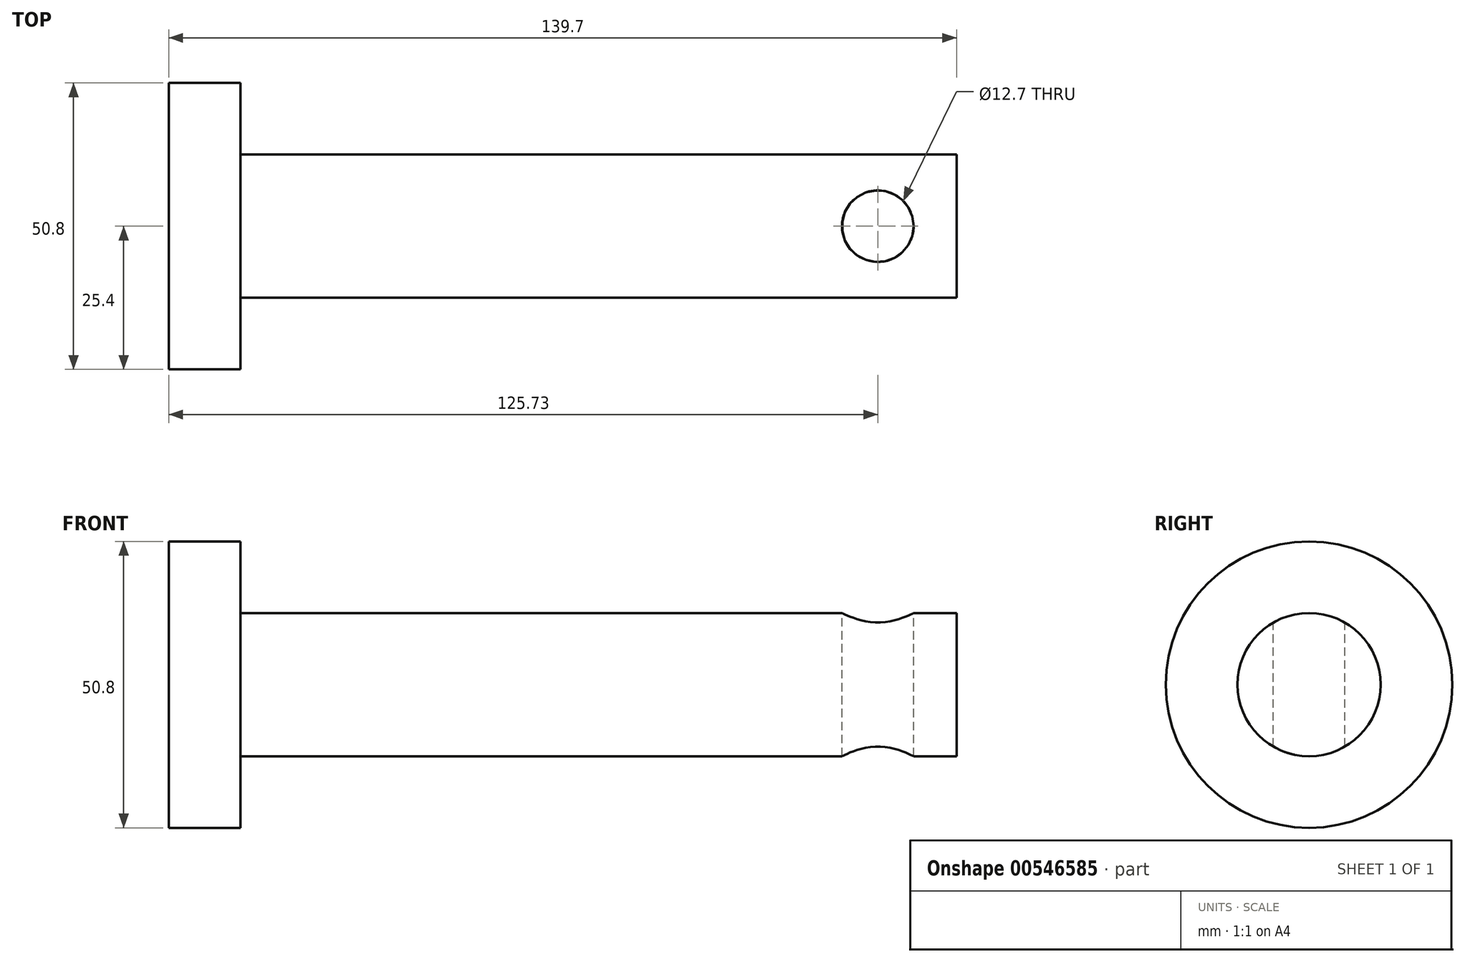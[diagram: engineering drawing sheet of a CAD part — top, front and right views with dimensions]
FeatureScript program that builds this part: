
annotation { "Feature Type Name" : "Feature", "Feature Type Description" : "" }
export const myFeature = defineFeature(function(context is Context, id is Id, definition is map)
    precondition{}
    {
        {
            var Q0;
            Q0=qCreatedBy(makeId("Right.planeOp"),FACE);
            var sketch = newSketch(context, id + "F0", { "sketchPlane" : qUnion([Q0])});
            skCircle(sketch, "E0", {"center": v(0, 0) * mm, "radius": 12.7 * mm});
            skSolve(sketch);
        }
        {
            var Q0;
            Q0 = qSketchRegion(id + "F0", true);
            extrude(context, id + "F1", {"entities" : qUnion([Q0]), "depth" : 127 * mm, "offsetDistance" : 25.4 * mm});
        }
        {
            var Q0;
            Q0=makeQuery(id+"F1.opExtrude","CAP_FACE",FACE,{"disambiguationData":[OSD([sQuery(id+"F0.wireOp",EDGE,"E0")])],"isStart":true});
            var sketch = newSketch(context, id + "F2", { "sketchPlane" : qUnion([Q0])});
            skCircle(sketch, "E1", {"center": v(0, 0) * mm, "radius": 25.4 * mm});
            skSolve(sketch);
        }
        {
            var Q0;
            Q0 = qSketchRegion(id + "F2", true);
            extrude(context, id + "F3", {"entities" : qUnion([Q0]), "operationType" : NewBodyOperationType.ADD, "depth" : 12.7 * mm, "offsetDistance" : 25.4 * mm});
        }
        {
            var Q0;
            Q0=qCreatedBy(makeId("Top.planeOp"),FACE);
            cPlane(context, id + "F4", {"entities" : qUnion([Q0]), "cplaneType" : CPlaneType.OFFSET, "offset" : 12.7 * mm, "width" : 152.4 * mm, "height" : 152.4 * mm});
        }
        {
            var Q0;
            Q0=qCreatedBy(id+"F4.planeOp",FACE);
            var sketch = newSketch(context, id + "F5", { "sketchPlane" : qUnion([Q0])});
            skCircle(sketch, "E2", {"center": v(113.03, 0) * mm, "radius": 6.35 * mm});
            skSolve(sketch);
        }
        {
            var Q0;
            Q0 = qSketchRegion(id + "F5", true);
            extrude(context, id + "F6", {"entities" : qUnion([Q0]), "operationType" : NewBodyOperationType.REMOVE, "endBound" : BoundingType.THROUGH_ALL, "oppositeDirection" : true, "depth" : 25.4 * mm, "offsetDistance" : 25.4 * mm});
        }
    });
